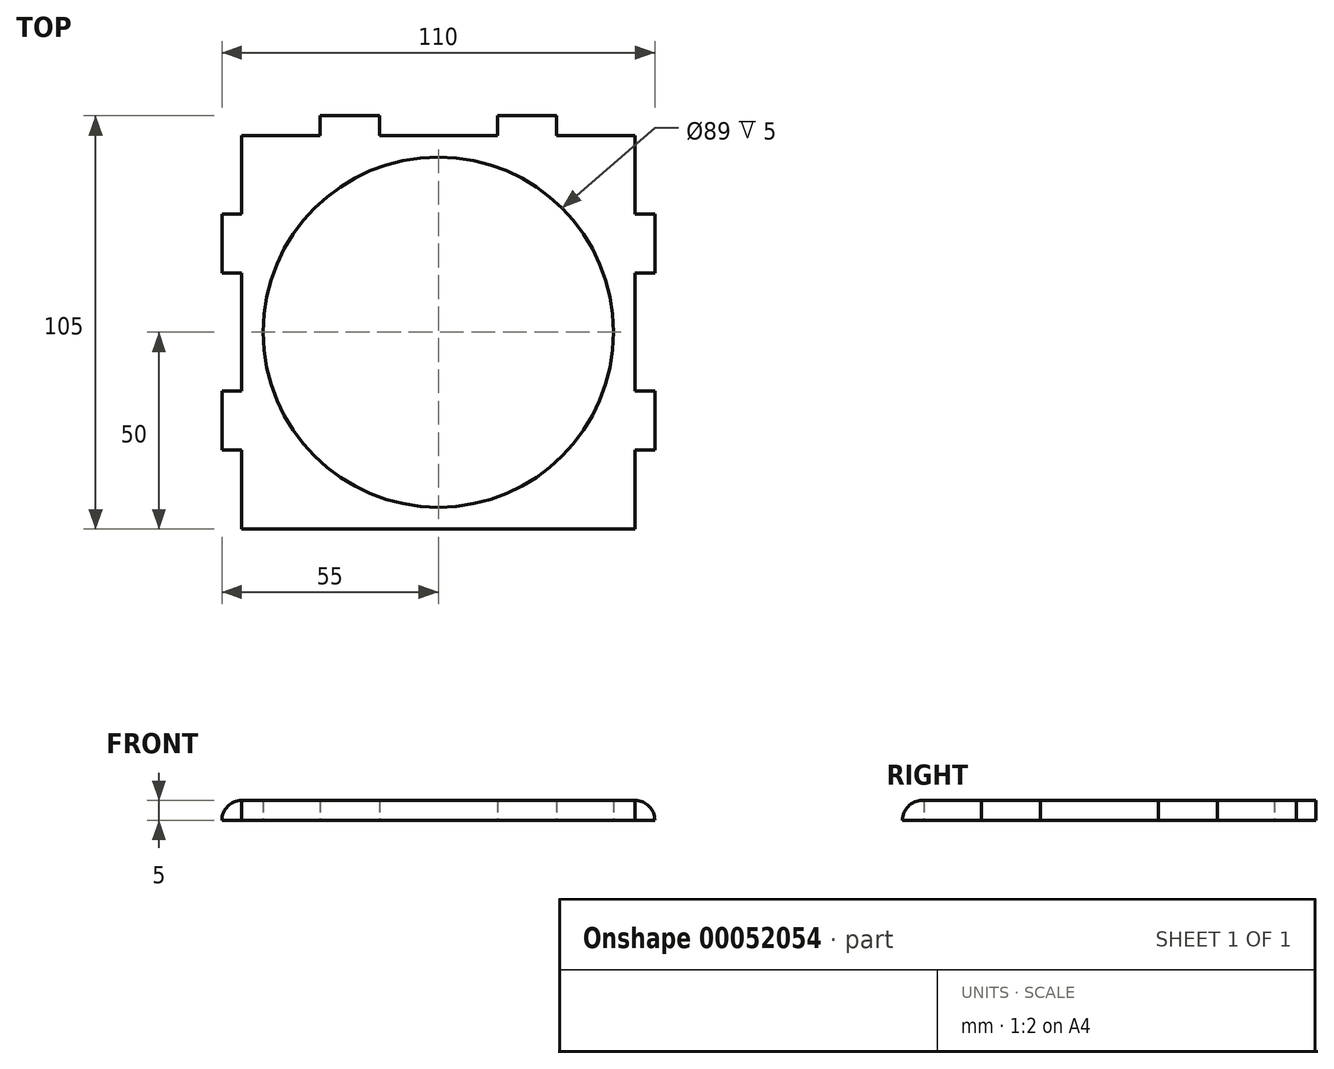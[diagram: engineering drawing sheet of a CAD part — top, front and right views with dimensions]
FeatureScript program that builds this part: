
annotation { "Feature Type Name" : "Feature", "Feature Type Description" : "" }
export const myFeature = defineFeature(function(context is Context, id is Id, definition is map)
    precondition{}
    {
        {
            var Q0;
            Q0=qCreatedBy(makeId("Top.planeOp"),FACE);
            var sketch = newSketch(context, id + "F0", { "sketchPlane" : qUnion([Q0])});
            skLineSegment(sketch, "E0.bottom", {"start": v(-50, 50) * mm, "end": v(-30, 50) * mm});
            skLineSegment(sketch, "E0.top", {"start": v(-50, -50) * mm, "end": v(50, -50) * mm});
            skLineSegment(sketch, "E0.left", {"start": v(-50, 50) * mm, "end": v(-50, 30) * mm});
            skLineSegment(sketch, "E0.right", {"start": v(50, 50) * mm, "end": v(50, 30) * mm});
            skLineSegment(sketch, "E1", {"start": v(-50, 50) * mm, "end": v(50, -50) * mm, "construction": true});
            skCircle(sketch, "E2", {"center": v(0, 0) * mm, "radius": 44.5 * mm});
            skLineSegment(sketch, "E3", {"start": v(-30, 50) * mm, "end": v(-30, 55) * mm});
            skLineSegment(sketch, "E4", {"start": v(-30, 55) * mm, "end": v(-15, 55) * mm});
            skLineSegment(sketch, "E5", {"start": v(-15, 55) * mm, "end": v(-15, 50) * mm});
            skLineSegment(sketch, "E6", {"start": v(15, 50) * mm, "end": v(15, 55) * mm});
            skLineSegment(sketch, "E7", {"start": v(15, 55) * mm, "end": v(30, 55) * mm});
            skLineSegment(sketch, "E8", {"start": v(30, 55) * mm, "end": v(30, 50) * mm});
            skLineSegment(sketch, "E9", {"start": v(0, -50) * mm, "end": v(0, 50) * mm, "construction": true});
            skLineSegment(sketch, "E10", {"start": v(-50, -30) * mm, "end": v(-55, -30) * mm});
            skLineSegment(sketch, "E11", {"start": v(-55, -30) * mm, "end": v(-55, -15) * mm});
            skLineSegment(sketch, "E12", {"start": v(-55, -15) * mm, "end": v(-50, -15) * mm});
            skLineSegment(sketch, "E13", {"start": v(-50, 30) * mm, "end": v(-55, 30) * mm});
            skLineSegment(sketch, "E14", {"start": v(-55, 30) * mm, "end": v(-55, 15) * mm});
            skLineSegment(sketch, "E15", {"start": v(-55, 15) * mm, "end": v(-50, 15) * mm});
            skLineSegment(sketch, "E16.MirrorCS", {"start": v(50, 30) * mm, "end": v(55, 30) * mm});
            skLineSegment(sketch, "E17.MirrorCS", {"start": v(55, 15) * mm, "end": v(50, 15) * mm});
            skLineSegment(sketch, "E18.MirrorCS", {"start": v(55, -15) * mm, "end": v(50, -15) * mm});
            skLineSegment(sketch, "E19.MirrorCS", {"start": v(50, -30) * mm, "end": v(55, -30) * mm});
            skLineSegment(sketch, "E20.MirrorCS", {"start": v(55, -30) * mm, "end": v(55, -15) * mm});
            skLineSegment(sketch, "E21.MirrorCS", {"start": v(55, 30) * mm, "end": v(55, 15) * mm});
            skLineSegment(sketch, "E22.trimOffspring", {"start": v(-15, 50) * mm, "end": v(15, 50) * mm});
            skLineSegment(sketch, "E23.trimOffspring", {"start": v(30, 50) * mm, "end": v(50, 50) * mm});
            skLineSegment(sketch, "E24.trimOffspring", {"start": v(50, 15) * mm, "end": v(50, -15) * mm});
            skLineSegment(sketch, "E25.trimOffspring", {"start": v(50, -30) * mm, "end": v(50, -50) * mm});
            skLineSegment(sketch, "E26.trimOffspring", {"start": v(-50, -30) * mm, "end": v(-50, -50) * mm});
            skLineSegment(sketch, "E27.trimOffspring", {"start": v(-50, 15) * mm, "end": v(-50, -15) * mm});
            skSolve(sketch);
        }
        {
            var Q0;
            {var subQ1=sQuery(id+"F0.wireOp",EDGE,"E0.top");Q0=makeQuery(id+"F0.imprint","IMPRINT",FACE,{"disambiguationData":[TD([[makeQuery(id+"F0.imprint","IMPRINT",EDGE,{"derivedFrom":subQ1}),1.0]])]});}
            var Q1;
            {var subQ4=sQuery(id+"F0.wireOp",EDGE,"E0.bottom");Q1=makeQuery(id+"F0.imprint","IMPRINT",FACE,{"disambiguationData":[TD([[makeQuery(id+"F0.imprint","IMPRINT",EDGE,{"derivedFrom":subQ4}),-1.0]])]});}
            extrude(context, id + "F1", {"entities" : qUnion([Q0, Q1]), "depth" : 5 * mm});
        }
        {
            var Q0;
            Q0=makeQuery(id+"F1.opExtrude","CAP_EDGE",EDGE,{"disambiguationData":[OSD([sQuery(id+"F0.wireOp",EDGE,"E0.top")])],"isStart":false});
            var Q1;
            Q1=makeQuery(id+"F1.opExtrude","CAP_EDGE",EDGE,{"disambiguationData":[OSD([sQuery(id+"F0.wireOp",EDGE,"E20.MirrorCS")])],"isStart":false});
            var Q2;
            Q2=makeQuery(id+"F1.opExtrude","CAP_EDGE",EDGE,{"disambiguationData":[OSD([sQuery(id+"F0.wireOp",EDGE,"E21.MirrorCS")])],"isStart":false});
            var Q3;
            Q3=makeQuery(id+"F1.opExtrude","CAP_EDGE",EDGE,{"disambiguationData":[OSD([sQuery(id+"F0.wireOp",EDGE,"E14")])],"isStart":false});
            var Q4;
            Q4=makeQuery(id+"F1.opExtrude","CAP_EDGE",EDGE,{"disambiguationData":[OSD([sQuery(id+"F0.wireOp",EDGE,"E11")])],"isStart":false});
            fillet(context, id + "F2", {"entities" : qUnion([Q0, Q1, Q2, Q3, Q4]), "radius" : 5 * mm, "tangentPropagation" : true, "allowEdgeOverflow" : false});
        }
    });
